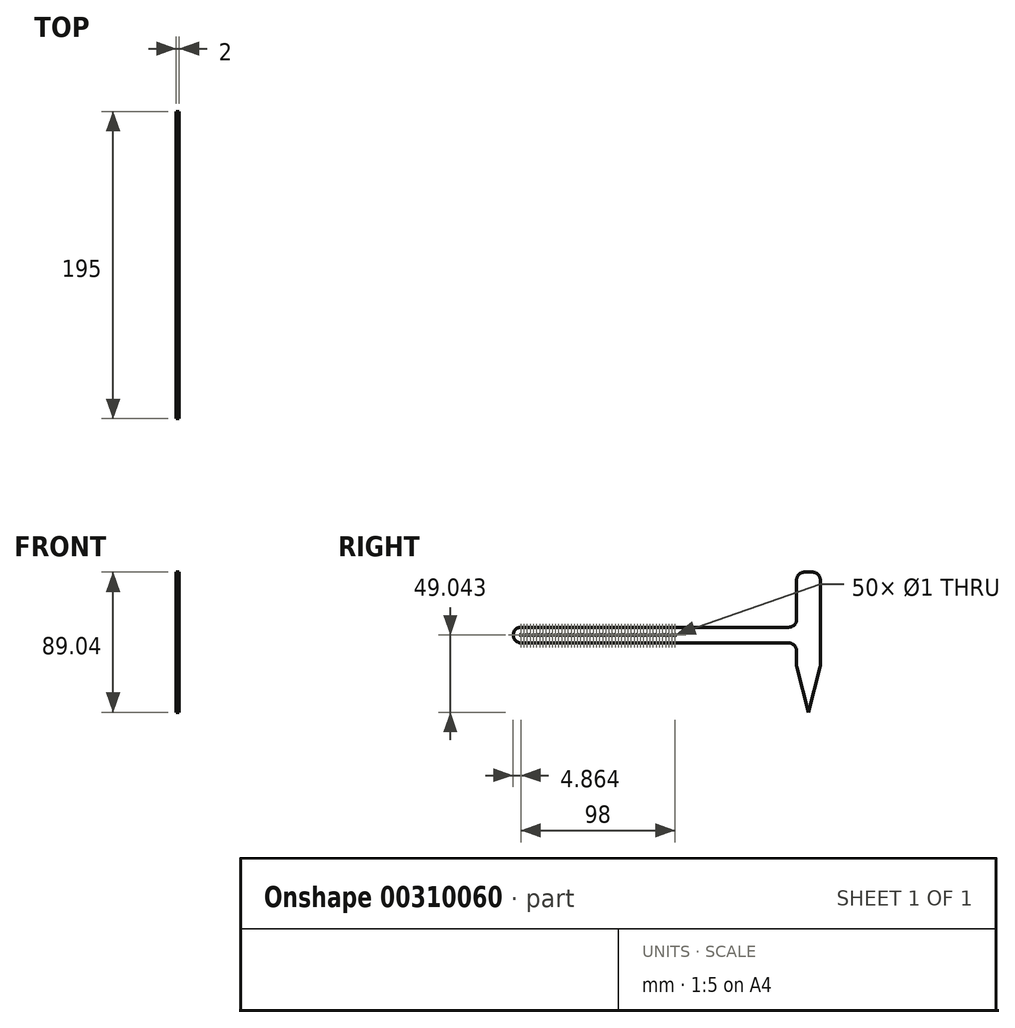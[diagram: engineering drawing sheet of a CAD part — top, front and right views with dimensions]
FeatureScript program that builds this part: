
annotation { "Feature Type Name" : "Feature", "Feature Type Description" : "" }
export const myFeature = defineFeature(function(context is Context, id is Id, definition is map)
    precondition{}
    {
        {
            var Q0;
            Q0=qCreatedBy(makeId("Right.planeOp"),FACE);
            var sketch = newSketch(context, id + "F0", { "sketchPlane" : qUnion([Q0])});
            skLineSegment(sketch, "E0.bottom", {"start": v(-101.64, 12.47) * mm, "end": v(78.36, 12.47) * mm});
            skLineSegment(sketch, "E0.top", {"start": v(-101.64, 2.47) * mm, "end": v(78.36, 2.47) * mm});
            skLineSegment(sketch, "E0.left", {"start": v(-101.64, 12.47) * mm, "end": v(-101.64, 2.47) * mm});
            skLineSegment(sketch, "E0.right", {"start": v(78.36, 12.47) * mm, "end": v(78.36, 2.47) * mm});
            skLineSegment(sketch, "E1.bottom", {"start": v(78.36, 47.47) * mm, "end": v(93.36, 47.47) * mm});
            skLineSegment(sketch, "E1.top", {"start": v(78.36, -12.53) * mm, "end": v(93.36, -12.53) * mm});
            skLineSegment(sketch, "E1.left", {"start": v(78.36, 47.47) * mm, "end": v(78.36, -12.53) * mm});
            skLineSegment(sketch, "E1.right", {"start": v(93.36, 47.47) * mm, "end": v(93.36, -12.53) * mm});
            skLineSegment(sketch, "E2", {"start": v(93.36, -12.53) * mm, "end": v(85.86, -41.57) * mm});
            skLineSegment(sketch, "E3", {"start": v(85.86, -41.57) * mm, "end": v(78.36, -12.53) * mm});
            skCircle(sketch, "E4", {"center": v(-96.78, 7.47) * mm, "radius": 0.5 * mm});
            skPoint(sketch, "E4.centerSnap0", {"position": v(-101.64, 7.47) * mm});
            skCircle(sketch, "E5.1.0.0", {"center": v(-94.78, 7.47) * mm, "radius": 0.5 * mm});
            skCircle(sketch, "E5.2.0.0", {"center": v(-92.78, 7.47) * mm, "radius": 0.5 * mm});
            skCircle(sketch, "E5.3.0.0", {"center": v(-90.78, 7.47) * mm, "radius": 0.5 * mm});
            skCircle(sketch, "E5.4.0.0", {"center": v(-88.78, 7.47) * mm, "radius": 0.5 * mm});
            skCircle(sketch, "E5.5.0.0", {"center": v(-86.78, 7.47) * mm, "radius": 0.5 * mm});
            skCircle(sketch, "E5.6.0.0", {"center": v(-84.78, 7.47) * mm, "radius": 0.5 * mm});
            skCircle(sketch, "E5.7.0.0", {"center": v(-82.78, 7.47) * mm, "radius": 0.5 * mm});
            skCircle(sketch, "E5.8.0.0", {"center": v(-80.78, 7.47) * mm, "radius": 0.5 * mm});
            skCircle(sketch, "E5.9.0.0", {"center": v(-78.78, 7.47) * mm, "radius": 0.5 * mm});
            skCircle(sketch, "E5.10.0.0", {"center": v(-76.78, 7.47) * mm, "radius": 0.5 * mm});
            skCircle(sketch, "E5.11.0.0", {"center": v(-74.78, 7.47) * mm, "radius": 0.5 * mm});
            skCircle(sketch, "E5.12.0.0", {"center": v(-72.78, 7.47) * mm, "radius": 0.5 * mm});
            skCircle(sketch, "E5.13.0.0", {"center": v(-70.78, 7.47) * mm, "radius": 0.5 * mm});
            skCircle(sketch, "E5.14.0.0", {"center": v(-68.78, 7.47) * mm, "radius": 0.5 * mm});
            skCircle(sketch, "E5.15.0.0", {"center": v(-66.78, 7.47) * mm, "radius": 0.5 * mm});
            skCircle(sketch, "E5.16.0.0", {"center": v(-64.78, 7.47) * mm, "radius": 0.5 * mm});
            skCircle(sketch, "E5.17.0.0", {"center": v(-62.78, 7.47) * mm, "radius": 0.5 * mm});
            skCircle(sketch, "E5.18.0.0", {"center": v(-60.78, 7.47) * mm, "radius": 0.5 * mm});
            skCircle(sketch, "E5.19.0.0", {"center": v(-58.78, 7.47) * mm, "radius": 0.5 * mm});
            skCircle(sketch, "E5.20.0.0", {"center": v(-56.78, 7.47) * mm, "radius": 0.5 * mm});
            skCircle(sketch, "E5.21.0.0", {"center": v(-54.78, 7.47) * mm, "radius": 0.5 * mm});
            skCircle(sketch, "E5.22.0.0", {"center": v(-52.78, 7.47) * mm, "radius": 0.5 * mm});
            skCircle(sketch, "E5.23.0.0", {"center": v(-50.78, 7.47) * mm, "radius": 0.5 * mm});
            skCircle(sketch, "E5.24.0.0", {"center": v(-48.78, 7.47) * mm, "radius": 0.5 * mm});
            skCircle(sketch, "E5.25.0.0", {"center": v(-46.78, 7.47) * mm, "radius": 0.5 * mm});
            skCircle(sketch, "E5.26.0.0", {"center": v(-44.78, 7.47) * mm, "radius": 0.5 * mm});
            skCircle(sketch, "E5.27.0.0", {"center": v(-42.78, 7.47) * mm, "radius": 0.5 * mm});
            skCircle(sketch, "E5.28.0.0", {"center": v(-40.78, 7.47) * mm, "radius": 0.5 * mm});
            skCircle(sketch, "E5.29.0.0", {"center": v(-38.78, 7.47) * mm, "radius": 0.5 * mm});
            skCircle(sketch, "E5.30.0.0", {"center": v(-36.78, 7.47) * mm, "radius": 0.5 * mm});
            skCircle(sketch, "E5.31.0.0", {"center": v(-34.78, 7.47) * mm, "radius": 0.5 * mm});
            skCircle(sketch, "E5.32.0.0", {"center": v(-32.78, 7.47) * mm, "radius": 0.5 * mm});
            skCircle(sketch, "E5.33.0.0", {"center": v(-30.78, 7.47) * mm, "radius": 0.5 * mm});
            skCircle(sketch, "E5.34.0.0", {"center": v(-28.78, 7.47) * mm, "radius": 0.5 * mm});
            skCircle(sketch, "E5.35.0.0", {"center": v(-26.78, 7.47) * mm, "radius": 0.5 * mm});
            skCircle(sketch, "E5.36.0.0", {"center": v(-24.78, 7.47) * mm, "radius": 0.5 * mm});
            skCircle(sketch, "E5.37.0.0", {"center": v(-22.78, 7.47) * mm, "radius": 0.5 * mm});
            skCircle(sketch, "E5.38.0.0", {"center": v(-20.78, 7.47) * mm, "radius": 0.5 * mm});
            skCircle(sketch, "E5.39.0.0", {"center": v(-18.78, 7.47) * mm, "radius": 0.5 * mm});
            skCircle(sketch, "E5.40.0.0", {"center": v(-16.78, 7.47) * mm, "radius": 0.5 * mm});
            skCircle(sketch, "E5.41.0.0", {"center": v(-14.78, 7.47) * mm, "radius": 0.5 * mm});
            skCircle(sketch, "E5.42.0.0", {"center": v(-12.78, 7.47) * mm, "radius": 0.5 * mm});
            skCircle(sketch, "E5.43.0.0", {"center": v(-10.78, 7.47) * mm, "radius": 0.5 * mm});
            skCircle(sketch, "E5.44.0.0", {"center": v(-8.78, 7.47) * mm, "radius": 0.5 * mm});
            skCircle(sketch, "E5.45.0.0", {"center": v(-6.78, 7.47) * mm, "radius": 0.5 * mm});
            skCircle(sketch, "E5.46.0.0", {"center": v(-4.78, 7.47) * mm, "radius": 0.5 * mm});
            skCircle(sketch, "E5.47.0.0", {"center": v(-2.78, 7.47) * mm, "radius": 0.5 * mm});
            skCircle(sketch, "E5.48.0.0", {"center": v(-0.78, 7.47) * mm, "radius": 0.5 * mm});
            skCircle(sketch, "E5.49.0.0", {"center": v(1.22, 7.47) * mm, "radius": 0.5 * mm});
            skLineSegment(sketch, "E5.direction1", {"start": v(-96.78, 7.47) * mm, "end": v(-94.78, 7.47) * mm, "construction": true});
            skSolve(sketch);
        }
        {
            var Q0;
            {var subQ1=sQuery(id+"F0.wireOp",EDGE,"E0.right");Q0=makeQuery(id+"F0.imprint","IMPRINT",FACE,{"disambiguationData":[TD([[makeQuery(id+"F0.imprint","IMPRINT",EDGE,{"derivedFrom":subQ1}),1.0]])]});}
            var Q1;
            Q1=makeQuery(id+"F0.imprint","IMPRINT",FACE,{"disambiguationData":[TD([[makeQuery(id+"F0.imprint","IMPRINT",EDGE,{"derivedFrom":sQuery(id+"F0.wireOp",EDGE,"E0.bottom")}),-1.0]])]});
            var Q2;
            Q2=makeQuery(id+"F0.imprint","IMPRINT",FACE,{"disambiguationData":[TD([[makeQuery(id+"F0.imprint","IMPRINT",EDGE,{"derivedFrom":sQuery(id+"F0.wireOp",EDGE,"E1.top")}),-1.0]])]});
            extrude(context, id + "F1", {"entities" : qUnion([Q0, Q1, Q2]), "depth" : 2 * mm});
        }
        {
            var Q0;
            Q0=makeQuery(id+"F1.opExtrude","SWEPT_EDGE",EDGE,{"disambiguationData":[OSD([sQuery(id+"F0.wireOp",EDGE,"E1.bottom"),sQuery(id+"F0.wireOp",EDGE,"E1.right")])]});
            var Q1;
            Q1=makeQuery(id+"F1.opExtrude","SWEPT_EDGE",EDGE,{"disambiguationData":[OSD([sQuery(id+"F0.wireOp",EDGE,"E1.bottom"),sQuery(id+"F0.wireOp",EDGE,"E1.left")])]});
            var Q2;
            Q2=makeQuery(id+"F1.opExtrude","SWEPT_EDGE",EDGE,{"disambiguationData":[OSD([sQuery(id+"F0.wireOp",EDGE,"E0.bottom"),sQuery(id+"F0.wireOp",EDGE,"E0.right"),sQuery(id+"F0.wireOp",EDGE,"E1.left")])]});
            var Q3;
            Q3=makeQuery(id+"F1.opExtrude","SWEPT_EDGE",EDGE,{"disambiguationData":[OSD([sQuery(id+"F0.wireOp",EDGE,"E0.top"),sQuery(id+"F0.wireOp",EDGE,"E0.right"),sQuery(id+"F0.wireOp",EDGE,"E1.left")])]});
            var Q4;
            Q4=makeQuery(id+"F1.opExtrude","SWEPT_EDGE",EDGE,{"disambiguationData":[OSD([sQuery(id+"F0.wireOp",EDGE,"E1.top"),sQuery(id+"F0.wireOp",EDGE,"E1.left"),sQuery(id+"F0.wireOp",EDGE,"E3")])]});
            var Q5;
            Q5=makeQuery(id+"F1.opExtrude","SWEPT_EDGE",EDGE,{"disambiguationData":[OSD([sQuery(id+"F0.wireOp",EDGE,"E1.top"),sQuery(id+"F0.wireOp",EDGE,"E1.right"),sQuery(id+"F0.wireOp",EDGE,"E2")])]});
            var Q6;
            Q6=makeQuery(id+"F1.opExtrude","SWEPT_EDGE",EDGE,{"disambiguationData":[OSD([sQuery(id+"F0.wireOp",EDGE,"E0.bottom"),sQuery(id+"F0.wireOp",EDGE,"E0.left")])]});
            var Q7;
            Q7=makeQuery(id+"F1.opExtrude","SWEPT_EDGE",EDGE,{"disambiguationData":[OSD([sQuery(id+"F0.wireOp",EDGE,"E0.top"),sQuery(id+"F0.wireOp",EDGE,"E0.left")])]});
            fillet(context, id + "F2", {"entities" : qUnion([Q0, Q1, Q2, Q3, Q4, Q5, Q6, Q7]), "radius" : 5 * mm, "tangentPropagation" : true, "allowEdgeOverflow" : false});
        }
    });
